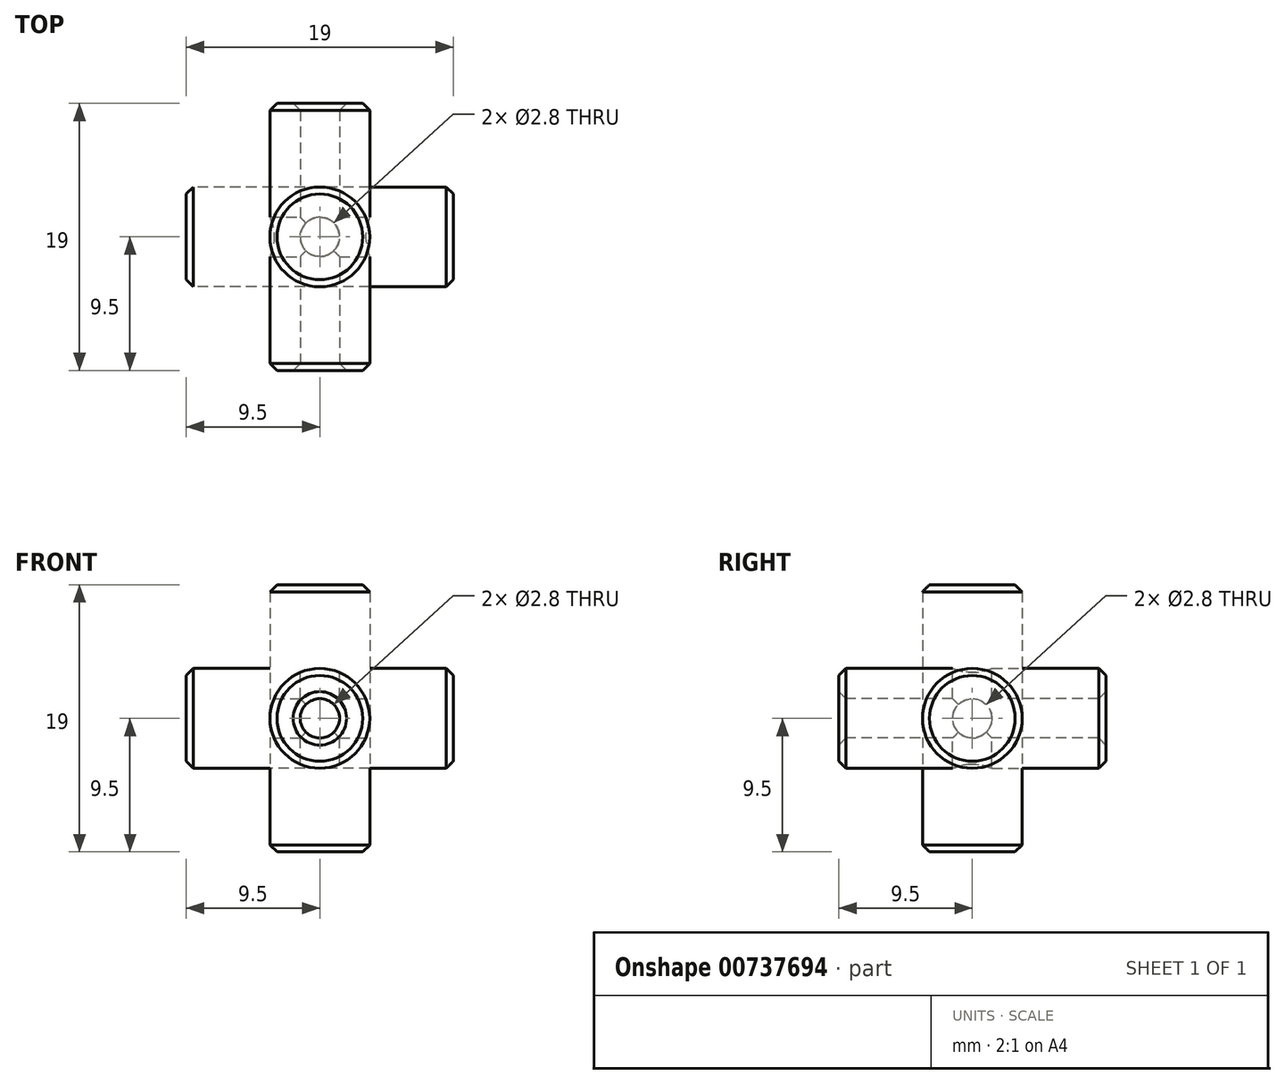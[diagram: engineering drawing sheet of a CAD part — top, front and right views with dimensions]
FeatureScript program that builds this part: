
annotation { "Feature Type Name" : "Feature", "Feature Type Description" : "" }
export const myFeature = defineFeature(function(context is Context, id is Id, definition is map)
    precondition{}
    {
        {
            var Q0;
            Q0=qCreatedBy(makeId("Front.planeOp"),FACE);
            var sketch = newSketch(context, id + "F0", { "sketchPlane" : qUnion([Q0])});
            skCircle(sketch, "E0", {"center": v(0, 0) * mm, "radius": 3.55 * mm});
            skSolve(sketch);
        }
        {
            var Q0;
            Q0=makeQuery(id+"F0.imprint","IMPRINT",FACE,{"disambiguationData":[TD([[makeQuery(id+"F0.imprint","IMPRINT",EDGE,{"derivedFrom":sQuery(id+"F0.wireOp",EDGE,"E0")}),1.0]])]});
            extrude(context, id + "F1", {"entities" : qUnion([Q0]), "endBound" : BoundingType.SYMMETRIC, "depth" : 19 * mm, "offsetDistance" : 25 * mm});
        }
        {
            var Q0;
            Q0=qCreatedBy(makeId("Front.planeOp"),FACE);
            var sketch = newSketch(context, id + "F2", { "sketchPlane" : qUnion([Q0])});
            skLineSegment(sketch, "E1.bottom", {"start": v(0, 0) * mm, "end": v(10, 0) * mm});
            skLineSegment(sketch, "E1.top", {"start": v(0, 10) * mm, "end": v(10, 10) * mm});
            skLineSegment(sketch, "E1.left", {"start": v(0, 0) * mm, "end": v(0, 10) * mm});
            skLineSegment(sketch, "E1.right", {"start": v(10, 0) * mm, "end": v(10, 10) * mm});
            skSolve(sketch);
        }
        {
            var Q0;
            Q0=makeQuery(id+"F2.imprint","IMPRINT",FACE,{"disambiguationData":[TD([[makeQuery(id+"F2.imprint","IMPRINT",EDGE,{"derivedFrom":sQuery(id+"F2.wireOp",EDGE,"E1.bottom")}),1.0]])]});
            extrude(context, id + "F3", {"entities" : qUnion([Q0]), "depth" : 10 * mm, "offsetDistance" : 25 * mm});
        }
        {
            var Q0;
            Q0=makeQuery(id+"F3.opExtrude","CAP_VERTEX",VERTEX,{"disambiguationData":[OSD([sQuery(id+"F2.wireOp",EDGE,"E1.top"),sQuery(id+"F2.wireOp",EDGE,"E1.left")])],"isStart":true});
            var Q1;
            Q1=makeQuery(id+"F3.opExtrude","CAP_VERTEX",VERTEX,{"disambiguationData":[OSD([sQuery(id+"F2.wireOp",EDGE,"E1.top"),sQuery(id+"F2.wireOp",EDGE,"E1.right")])],"isStart":false});
            var Q2;
            Q2=makeQuery(id+"F3.opExtrude","CAP_VERTEX",VERTEX,{"disambiguationData":[OSD([sQuery(id+"F2.wireOp",EDGE,"E1.bottom"),sQuery(id+"F2.wireOp",EDGE,"E1.right")])],"isStart":false});
            cPlane(context, id + "F4", {"entities" : qUnion([Q0, Q1, Q2]), "cplaneType" : CPlaneType.THREE_POINT, "offset" : 25 * mm, "width" : 150 * mm, "height" : 150 * mm});
        }
        {
            var Q0;
            Q0=qCreatedBy(id+"F4.planeOp",FACE);
            var sketch = newSketch(context, id + "F5", { "sketchPlane" : qUnion([Q0])});
            skLineSegment(sketch, "E2", {"start": v(0, 0) * mm, "end": v(14.14, 10) * mm});
            skSolve(sketch);
        }
        {
            var Q0;
            Q0=makeQuery(id+"F1.opExtrude","SWEPT_BODY",BODY,{"disambiguationData":[OSD([sQuery(id+"F0.wireOp",EDGE,"E0")])]});
            var Q1;
            Q1=sQuery(id+"F5.wireOp",EDGE,"E2");
            circularPattern(context, id + "F6", {"entities" : qUnion([Q0]), "axis" : qUnion([Q1]), "angle" : 360 * degree, "instanceCount" : 3, "equalSpace" : true});
        }
        {
            var Q0;
            Q0=makeQuery(id+"F3.opExtrude","SWEPT_BODY",BODY,{"disambiguationData":[OSD([sQuery(id+"F2.wireOp",EDGE,"E1.bottom"),sQuery(id+"F2.wireOp",EDGE,"E1.top"),sQuery(id+"F2.wireOp",EDGE,"E1.left"),sQuery(id+"F2.wireOp",EDGE,"E1.right")])]});
            deleteBodies(context, id + "F7", {"entities" : qUnion([Q0])});
        }
        {
            var Q0;
            Q0=qCreatedBy(makeId("Front.planeOp"),FACE);
            var sketch = newSketch(context, id + "F8", { "sketchPlane" : qUnion([Q0])});
            skCircle(sketch, "E3", {"center": v(0, 0) * mm, "radius": 1.4 * mm});
            skSolve(sketch);
        }
        {
            var Q0;
            Q0 = qSketchRegion(id + "F8", true);
            extrude(context, id + "F9", {"entities" : qUnion([Q0]), "endBound" : BoundingType.SYMMETRIC, "oppositeDirection" : true, "depth" : 25 * mm, "offsetDistance" : 25 * mm});
        }
        {
            var Q0;
            Q0=makeQuery(id+"F9.opExtrude","SWEPT_BODY",BODY,{"disambiguationData":[OSD([sQuery(id+"F8.wireOp",EDGE,"E3")])]});
            var Q1;
            Q1=sQuery(id+"F5.wireOp",EDGE,"E2");
            circularPattern(context, id + "F10", {"entities" : qUnion([Q0]), "axis" : qUnion([Q1]), "angle" : 360 * degree, "instanceCount" : 3, "equalSpace" : true});
        }
        {
            var Q0;
            Q0=makeQuery(id+"F9.opExtrude","SWEPT_BODY",BODY,{"disambiguationData":[OSD([sQuery(id+"F8.wireOp",EDGE,"E3")])]});
            var Q1;
            Q1=makeQuery(id+"F10.opPattern","COPY",BODY,{"derivedFrom":makeQuery(id+"F9.opExtrude","SWEPT_BODY",BODY,{"disambiguationData":[OSD([sQuery(id+"F8.wireOp",EDGE,"E3")])]}),"instanceName":"2"});
            var Q2;
            Q2=makeQuery(id+"F10.opPattern","COPY",BODY,{"derivedFrom":makeQuery(id+"F9.opExtrude","SWEPT_BODY",BODY,{"disambiguationData":[OSD([sQuery(id+"F8.wireOp",EDGE,"E3")])]}),"instanceName":"1"});
            var Q3;
            Q3=makeQuery(id+"F1.opExtrude","SWEPT_BODY",BODY,{"disambiguationData":[OSD([sQuery(id+"F0.wireOp",EDGE,"E0")])]});
            booleanBodies(context, id + "F11", {"operationType" : BooleanOperationType.SUBTRACTION, "tools" : qUnion([Q0, Q1, Q2]), "targets" : qUnion([Q3])});
        }
        {
            var Q0;
            Q0=makeQuery(id+"F6.opPattern","COPY",FACE,{"derivedFrom":makeQuery(id+"F1.opExtrude","CAP_FACE",FACE,{"disambiguationData":[OSD([sQuery(id+"F0.wireOp",EDGE,"E0")])],"isStart":false}),"instanceName":"2"});
            var Q1;
            Q1=makeQuery(id+"F6.opPattern","COPY",FACE,{"derivedFrom":makeQuery(id+"F1.opExtrude","CAP_FACE",FACE,{"disambiguationData":[OSD([sQuery(id+"F0.wireOp",EDGE,"E0")])],"isStart":true}),"instanceName":"2"});
            var Q2;
            Q2=makeQuery(id+"F6.opPattern","COPY",FACE,{"derivedFrom":makeQuery(id+"F1.opExtrude","CAP_FACE",FACE,{"disambiguationData":[OSD([sQuery(id+"F0.wireOp",EDGE,"E0")])],"isStart":false}),"instanceName":"1"});
            var Q3;
            Q3=makeQuery(id+"F6.opPattern","COPY",FACE,{"derivedFrom":makeQuery(id+"F1.opExtrude","CAP_FACE",FACE,{"disambiguationData":[OSD([sQuery(id+"F0.wireOp",EDGE,"E0")])],"isStart":true}),"instanceName":"1"});
            var Q4;
            Q4=makeQuery(id+"F1.opExtrude","CAP_FACE",FACE,{"disambiguationData":[OSD([sQuery(id+"F0.wireOp",EDGE,"E0")])],"isStart":true});
            var Q5;
            Q5=makeQuery(id+"F1.opExtrude","CAP_FACE",FACE,{"disambiguationData":[OSD([sQuery(id+"F0.wireOp",EDGE,"E0")])],"isStart":false});
            chamfer(context, id + "F12", {"entities" : qUnion([Q0, Q1, Q2, Q3, Q4, Q5]), "width" : 0.5 * mm, "tangentPropagation" : true});
        }
    });
